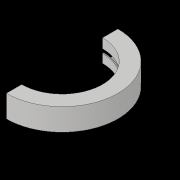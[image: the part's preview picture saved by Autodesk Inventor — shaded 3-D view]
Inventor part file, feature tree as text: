
AUTODESK INVENTOR PART (.ipt)
format: ipt  version: 2017 (Build 210142000, 142)  size: 113,152 bytes
history: native  units: in
note: dims shown in document units (in); Inventor stores cm internally (conversion verified against a paired STEP export)
features: revolve x1, sketch x1
ambient origin geometry x8: Origin, YZ Plane, XZ Plane, XY Plane, X Axis, Y Axis, Z Axis, Center Point
bodies: Solid1 (feature_tree)
feature tree (2):
  revolve  "Revolution1"  [1 undecoded]
  sketch  "Sketch1"  dims[d0=2.0in d2=10.5in d3=2.0in d4=2.875in d5=0.125in d6=0.125in d7=0.125in d8=0.125in d9=0.125in d10=0.125in d11=0.125in d12=0.125in d13=1.0285in d14=0.5in d15=180.0deg d16=5.25in d17=0.125in d18=0.125in]
note: 1 required parameter value undecoded (feature->parameter linkage not recoverable at this tier; creation-order binding heuristic only, values carry confidence <= 0.55)
